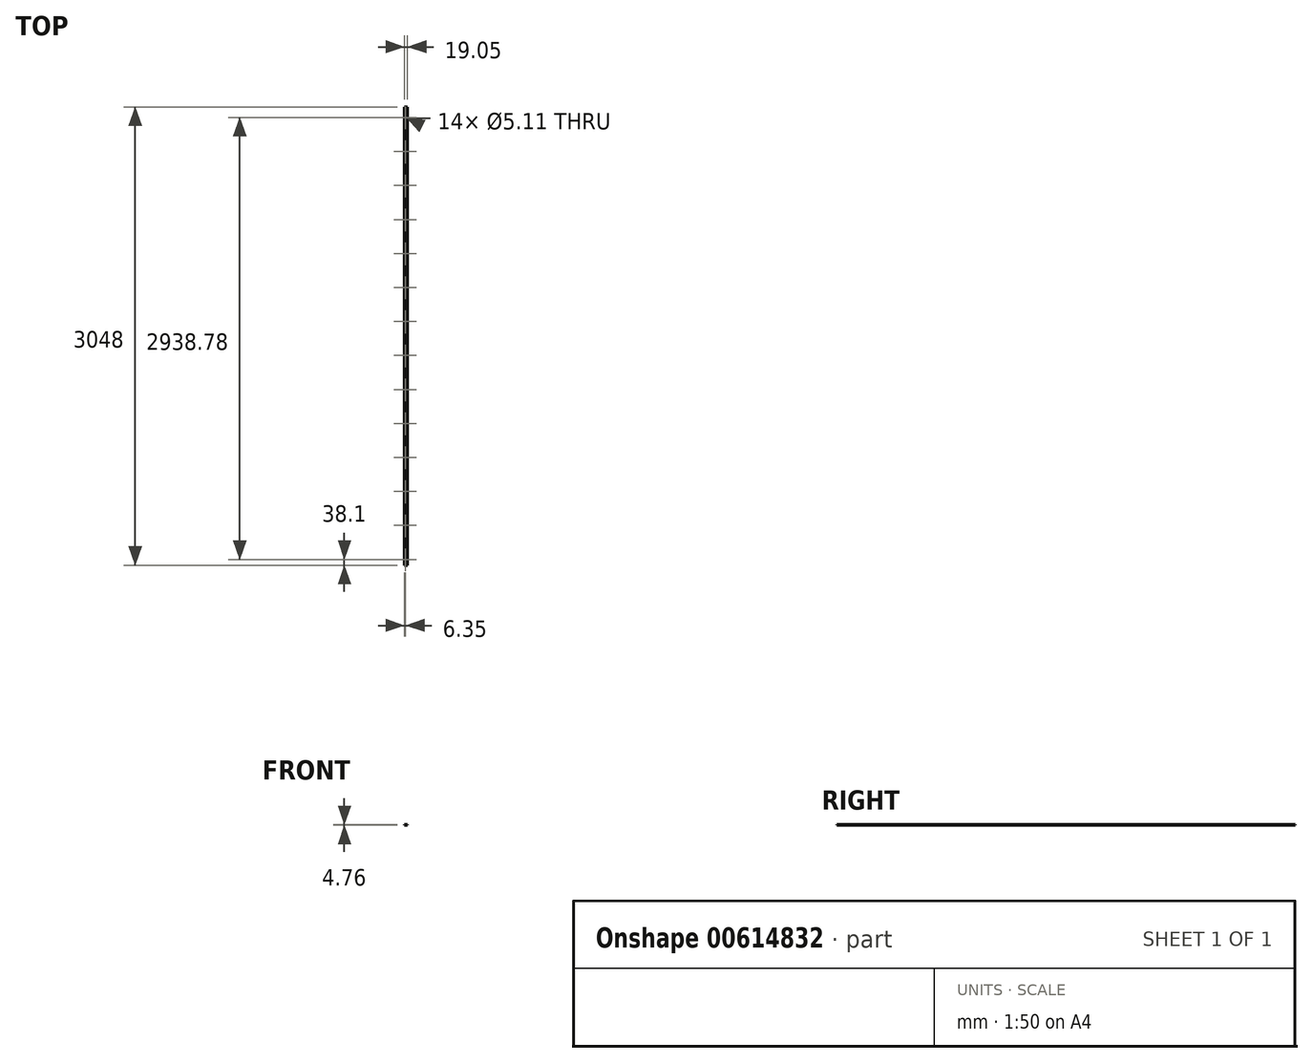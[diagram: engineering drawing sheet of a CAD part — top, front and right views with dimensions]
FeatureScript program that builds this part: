
annotation { "Feature Type Name" : "Feature", "Feature Type Description" : "" }
export const myFeature = defineFeature(function(context is Context, id is Id, definition is map)
    precondition{}
    {
        {
            var Q0;
            Q0=qCreatedBy(makeId("Front.planeOp"),FACE);
            var sketch = newSketch(context, id + "F0", { "sketchPlane" : qUnion([Q0])});
            skLineSegment(sketch, "E0.bottom", {"start": v(0, 0) * mm, "end": v(19.05, 0) * mm});
            skLineSegment(sketch, "E0.top", {"start": v(0, 4.76) * mm, "end": v(19.05, 4.76) * mm});
            skLineSegment(sketch, "E0.left", {"start": v(0, 0) * mm, "end": v(0, 4.76) * mm});
            skLineSegment(sketch, "E0.right", {"start": v(19.05, 0) * mm, "end": v(19.05, 4.76) * mm});
            skSolve(sketch);
        }
        {
            var Q0;
            Q0=makeQuery(id+"F0.imprint","IMPRINT",FACE,{"disambiguationData":[TD([[makeQuery(id+"F0.imprint","IMPRINT",EDGE,{"derivedFrom":sQuery(id+"F0.wireOp",EDGE,"E0.bottom")}),1.0]])]});
            extrude(context, id + "F1", {"entities" : qUnion([Q0]), "endBound" : BoundingType.SYMMETRIC, "depth" : 3048 * mm, "offsetDistance" : 25.4 * mm});
        }
        {
            var Q0;
            Q0=makeQuery(id+"F1.opExtrude","SWEPT_FACE",FACE,{"disambiguationData":[OSD([sQuery(id+"F0.wireOp",EDGE,"E0.top")])]});
            var sketch = newSketch(context, id + "F2", { "sketchPlane" : qUnion([Q0])});
            skPoint(sketch, "E1", {"position": v(6.35, -1485.9) * mm});
            skPoint(sketch, "E2.0.1.0", {"position": v(6.35, -1259.84) * mm});
            skPoint(sketch, "E2.0.2.0", {"position": v(6.35, -1033.78) * mm});
            skPoint(sketch, "E2.0.3.0", {"position": v(6.35, -807.72) * mm});
            skPoint(sketch, "E2.0.4.0", {"position": v(6.35, -581.66) * mm});
            skPoint(sketch, "E2.0.5.0", {"position": v(6.35, -355.6) * mm});
            skPoint(sketch, "E2.0.6.0", {"position": v(6.35, -129.54) * mm});
            skPoint(sketch, "E2.0.7.0", {"position": v(6.35, 96.52) * mm});
            skPoint(sketch, "E2.0.8.0", {"position": v(6.35, 322.58) * mm});
            skPoint(sketch, "E2.0.9.0", {"position": v(6.35, 548.64) * mm});
            skPoint(sketch, "E2.0.10.0", {"position": v(6.35, 774.7) * mm});
            skPoint(sketch, "E2.0.11.0", {"position": v(6.35, 1000.76) * mm});
            skPoint(sketch, "E2.0.12.0", {"position": v(6.35, 1226.82) * mm});
            skPoint(sketch, "E2.0.13.0", {"position": v(6.35, 1452.88) * mm});
            skLineSegment(sketch, "E2.direction1", {"start": v(6.35, -1485.9) * mm, "end": v(31.75, -1485.9) * mm, "construction": true});
            skLineSegment(sketch, "E2.direction2", {"start": v(6.35, -1485.9) * mm, "end": v(6.35, -1259.84) * mm, "construction": true});
            skSolve(sketch);
        }
        {
            var Q0;
            Q0=sQuery(id+"F2.wireOp",VERTEX,"E2.0.13.0");
            var Q1;
            Q1=sQuery(id+"F2.wireOp",VERTEX,"E2.0.12.0");
            var Q2;
            Q2=sQuery(id+"F2.wireOp",VERTEX,"E2.0.10.0");
            var Q3;
            Q3=sQuery(id+"F2.wireOp",VERTEX,"E2.0.11.0");
            var Q4;
            Q4=sQuery(id+"F2.wireOp",VERTEX,"E2.0.3.0");
            var Q5;
            Q5=sQuery(id+"F2.wireOp",VERTEX,"E2.0.4.0");
            var Q6;
            Q6=sQuery(id+"F2.wireOp",VERTEX,"E2.0.5.0");
            var Q7;
            Q7=sQuery(id+"F2.wireOp",VERTEX,"E2.0.9.0");
            var Q8;
            Q8=sQuery(id+"F2.wireOp",VERTEX,"E2.0.6.0");
            var Q9;
            Q9=sQuery(id+"F2.wireOp",VERTEX,"E2.0.7.0");
            var Q10;
            Q10=sQuery(id+"F2.wireOp",VERTEX,"E2.0.8.0");
            var Q11;
            Q11=sQuery(id+"F2.wireOp",VERTEX,"E2.direction1.end");
            var Q12;
            Q12=sQuery(id+"F2.wireOp",VERTEX,"E1");
            var Q13;
            Q13=sQuery(id+"F2.wireOp",VERTEX,"E2.0.1.0");
            var Q14;
            Q14=sQuery(id+"F2.wireOp",VERTEX,"E2.0.2.0");
            var Q15;
            Q15=makeQuery(id+"F1.opExtrude","SWEPT_BODY",BODY,{"disambiguationData":[OSD([sQuery(id+"F0.wireOp",EDGE,"E0.bottom"),sQuery(id+"F0.wireOp",EDGE,"E0.top"),sQuery(id+"F0.wireOp",EDGE,"E0.left"),sQuery(id+"F0.wireOp",EDGE,"E0.right")])]});
            hole(context, id + "F3", {"style" : HoleStyle.C_SINK, "endStyle" : HoleEndStyle.THROUGH, "standardTappedOrClearance" : lookupTablePath({ "standard" : "ANSI", "fit" : "Normal (ASME)", "size" : "#10", "type" : "Clearance" }), "standardBlindInLast" : lookupTablePath({ "fit" : "Free", "standard" : "ANSI", "size" : "#10", "type" : "Clearance" }), "holeDiameter" : 5.1 * mm, "cSinkDiameter" : 10.44 * mm, "cSinkAngle" : 82 * degree, "majorDiameter" : 4.83 * mm, "tappedDepth" : 16.5 * mm, "tapClearance" : 3, "startFromSketch" : true, "locations" : qUnion([Q0, Q1, Q2, Q3, Q4, Q5, Q6, Q7, Q8, Q9, Q10, Q11, Q12, Q13, Q14]), "scope" : qUnion([Q15])});
        }
    });
